# Revit family: DIVITYP001
name_source: partatom
category: Furniture
units: mm (PartAtom-declared; Revit-internal decimal feet)

## family parameters
Always vertical = Yes
Cut with Voids When Loaded = No
OmniClass Number = 23.40.20.00
OmniClass Title = General Furniture and Specialties
Render Appearance Source = Family Geometry
Room Calculation Point = No
Shared = No
Work Plane-Based = No

## types (1)
- DIVITYP001
    Cost = 87676 $
    Default Elevation = 0 mm  [stored 0 ft]
    Description = 5 x Essex Mid Back Task Chair - Express, 2 x REVERE - BLACK MESH BACK - BLACK SEAT FABRIC, 2 x Desktop Organizer - White, 1 x Suspended Caddy - White, 2 x Hidden Drawer BF Ped MOBILE with CUSHION 12W, 2 x CALIBRATE EXTEND HUTCH WALL BRACKET, 1 x DiVi LINEAR HARD PANEL-PWR-PERM MONO- 50H X 48W, 3 x DiVi LINEAR Hard PANEL -NPWR-PERM MONO- 50H X 72W, 3 x DiVi LINEAR Hard PANEL -NPWR-PERM MONO- 58H X 72W, 1 x Divi Gallery Panel Mid-Mount Wing - 50H x 72W RH Horz, 2 x Divi Gallery Panel End Double - 58H x 60W Horz, 1 x Divi Gallery Panel Mid-Mount - 50H x 30W LH Horz, 1 x Divi Gallery Panel  Spine Dbl - 50H x 60W Horz, 1 x Divi Gallery Panel Wing RH - 50H x 30W Horz, 1 x POST FILLER DiVi LINEAR 4 WAY 58"H, 2 x DIVI LINEAR BASE RACEWAY SHROUD END OF RUN, 1 x DIVI LINEAR BASE RACEWAY SHROUD END OF RUN, 1 x Box/File Lateral L Series R Pull 30", 1 x Wardrobe Tower Right Lseries B/B/F W/Side Bookshelf 49"H, 1 x TBL, REC, 2mm, 24Dx72Wx29H, HAL, E SERIES GLD 2 STAGE, 1 x TBL, REC, 2MM, 30DX72WX29H, HAL, E SERIES GLD 2 STAGE, 1 x TBL, 120, 2mm, 24Dx4848Wx29H, HAL, GLD, 1 x TBL, 120, 2mm, 24Dx5454Wx29H, HAL, GLD, 1 x Rectangular - 2mm Edge - 24D x 24W, 1 x Rectangular - 2mm Edge - 24D x 60W, 1 x Rectangular - 2mm Edge - 30D x 72W, 1 x 120C 90L 90R Corner - 2mm Edge - 24D x 48W, 1 x O-LEG 27" X 30" DiVi MOUNT LH, 4 x 2.5 X 2.5 WS POST SUPPORT PILLAR 7"H, 2 x Regular Cantilever - Left Hand - 24D, 1 x Regular Cantilever - Left Hand - 30D, 1 x Regular Cantilever - Right Hand - 30D, 1 x CBX Full Depth BBF Ped 24Dx28Hx24W, 1 x CBX Combo B/F Ped Left/Bookcase Right 18D x 21H x 30D, 1 x CBX Combo B/F Ped Right/Bookcase Left 18D x 21H x 36D, 1 x CBX BF HAT BASE 24" Left, 1 x Cbx Full Depth Lat Bf 24dx21hx36w, 1 x CBX BBF Ped Tower with Cupboard Hinge Right 24Dx50Hx12W, 1 x DV BBF Ped Towers W/ Open Side LH 58H x 24D x 16W, 6 x Rectangular Pull Handle with Paint Options, 1 x Cbx Stack On Bookcase 14dx37hx18w, 1 x CBX Suspended Utility Powered - Condition A, 1 x Cbx Open Side Bf Wardrobe Lh 24dx50hx24w, 1 x Cbx Open Side Ff Wardrobe Rh 24dx50hx24w, 1 x Divi Channel Screen, Panel Top, 3/8" Glass, 8hx48w, 3 x Divi Channel Screen, Panel Top,3/8" Glass,12hx72w, 1 x Channel Scrn,GP Side,PET,Dim S,SMnt,Uni,50hx24w
    Exported From CET Designer = Yes
    Manufacturer = AIS
    Model = 4871
    Show DIVITYP001 = Yes
    VisibilityIndex = 0

note: [stored X ft] marks values corroborated as IEEE doubles in the binary element streams (Revit-internal decimal feet)

## geometry (parser evidence)
native form markers: Sweep x2
no freeform markers — native parametric forms only
